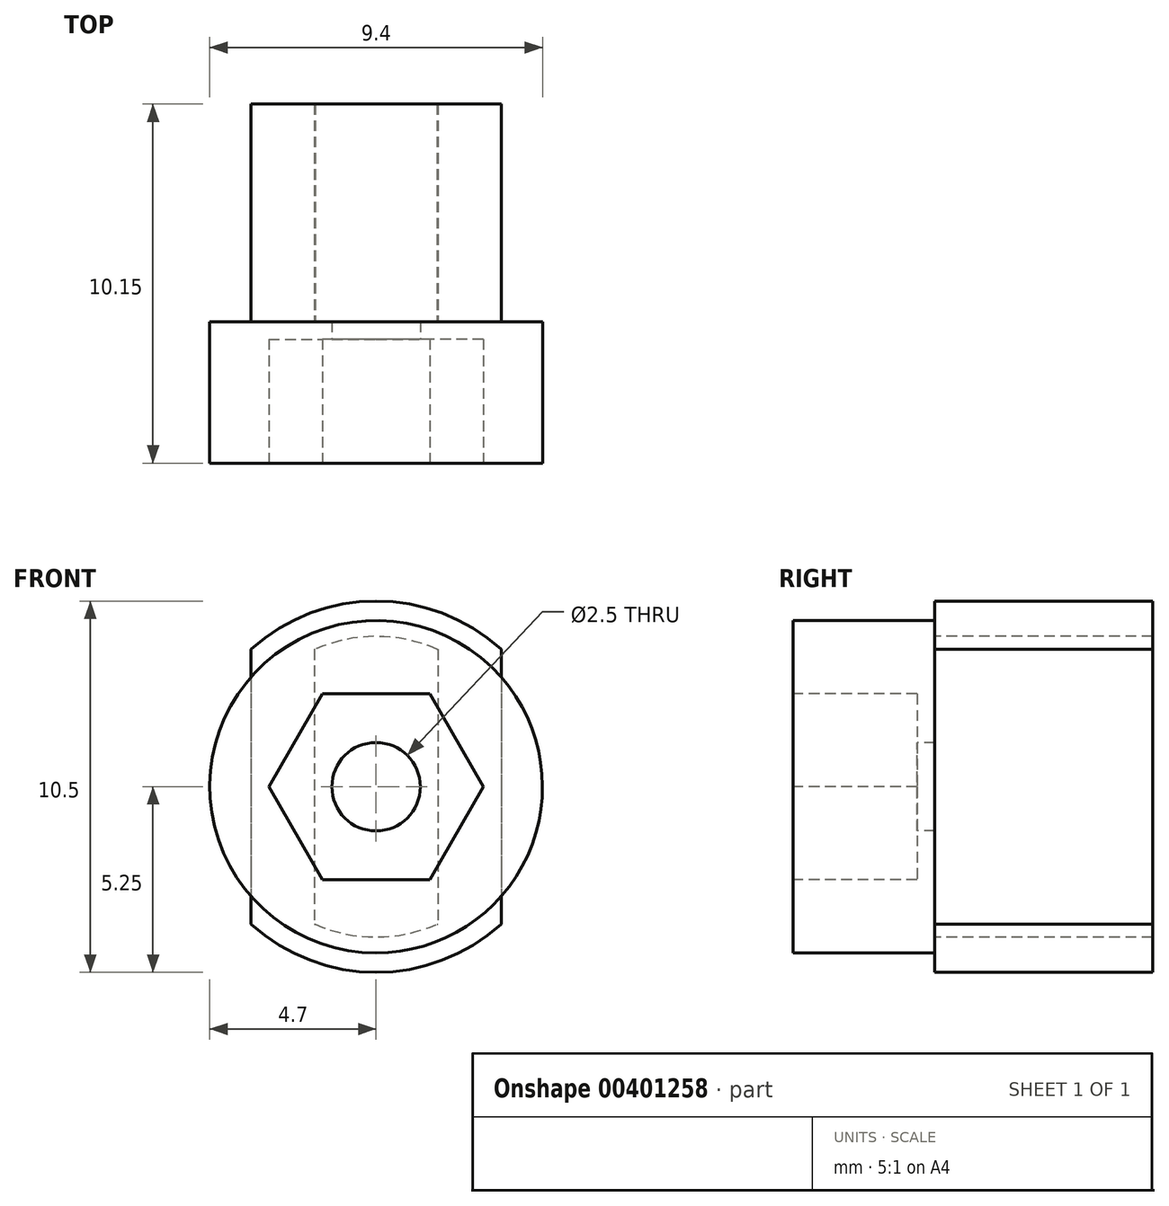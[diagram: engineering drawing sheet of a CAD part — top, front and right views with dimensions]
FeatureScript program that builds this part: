
annotation { "Feature Type Name" : "Feature", "Feature Type Description" : "" }
export const myFeature = defineFeature(function(context is Context, id is Id, definition is map)
    precondition{}
    {
        {
            var Q0;
            Q0=qCreatedBy(makeId("Front.planeOp"),FACE);
            var sketch = newSketch(context, id + "F0", { "sketchPlane" : qUnion([Q0])});
            skCircle(sketch, "E0", {"center": v(0, 0) * mm, "radius": 5.25 * mm});
            skCircle(sketch, "E1", {"center": v(0, 0) * mm, "radius": 4.25 * mm});
            skLineSegment(sketch, "E2.bottom", {"start": v(-1.75, 4.95) * mm, "end": v(1.75, 4.95) * mm});
            skLineSegment(sketch, "E2.top", {"start": v(-1.75, -4.95) * mm, "end": v(1.75, -4.95) * mm});
            skLineSegment(sketch, "E2.left", {"start": v(-1.75, 4.95) * mm, "end": v(-1.75, -4.95) * mm});
            skLineSegment(sketch, "E2.right", {"start": v(1.75, 4.95) * mm, "end": v(1.75, -4.95) * mm});
            skLineSegment(sketch, "E3.bottom", {"start": v(-3.53, 3.88) * mm, "end": v(3.53, 3.88) * mm});
            skLineSegment(sketch, "E3.top", {"start": v(-3.53, -3.88) * mm, "end": v(3.53, -3.88) * mm});
            skLineSegment(sketch, "E3.left", {"start": v(-3.53, 3.88) * mm, "end": v(-3.53, -3.88) * mm});
            skLineSegment(sketch, "E3.right", {"start": v(3.53, 3.88) * mm, "end": v(3.53, -3.88) * mm});
            skSolve(sketch);
        }
        {
            var Q0;
            {var subQ0=sQuery(id+"F0.wireOp",EDGE,"E2.left");var subQ3=sQuery(id+"F0.wireOp",EDGE,"E3.bottom");var subQ5=makeQuery(id+"F0.imprint","INTERSECT",VERTEX,{"derivedFrom":[subQ0,subQ3]});Q0=makeQuery(id+"F0.imprint","IMPRINT",FACE,{"disambiguationData":[TD([[makeQuery(id+"F0.imprint","IMPRINT",EDGE,{"disambiguationData":[TD([[subQ5,1.0]])],"derivedFrom":subQ0}),-1.0]])]});}
            var Q1;
            {var subQ0=sQuery(id+"F0.wireOp",EDGE,"E2.left");var subQ1=sQuery(id+"F0.wireOp",EDGE,"E1");var subQ2=makeQuery(id+"F0.imprint","INTERSECT",VERTEX,{"disambiguationData":[OD(0.0)],"derivedFrom":[subQ1,subQ0]});Q1=makeQuery(id+"F0.imprint","IMPRINT",FACE,{"disambiguationData":[TD([[makeQuery(id+"F0.imprint","IMPRINT",EDGE,{"disambiguationData":[TD([[subQ2,-1.0]])],"derivedFrom":subQ1}),-1.0]])]});}
            var Q2;
            {var subQ0=sQuery(id+"F0.wireOp",EDGE,"E2.left");var subQ1=sQuery(id+"F0.wireOp",EDGE,"E1");var subQ2=makeQuery(id+"F0.imprint","INTERSECT",VERTEX,{"disambiguationData":[OD(0.0)],"derivedFrom":[subQ1,subQ0]});Q2=makeQuery(id+"F0.imprint","IMPRINT",FACE,{"disambiguationData":[TD([[makeQuery(id+"F0.imprint","IMPRINT",EDGE,{"disambiguationData":[TD([[subQ2,-1.0]])],"derivedFrom":subQ1}),1.0]])]});}
            var Q3;
            {var subQ0=sQuery(id+"F0.wireOp",EDGE,"E3.left");var subQ1=sQuery(id+"F0.wireOp",EDGE,"E1");var subQ2=makeQuery(id+"F0.imprint","INTERSECT",VERTEX,{"disambiguationData":[OD(1.0)],"derivedFrom":[subQ1,subQ0]});Q3=makeQuery(id+"F0.imprint","IMPRINT",FACE,{"disambiguationData":[TD([[makeQuery(id+"F0.imprint","IMPRINT",EDGE,{"disambiguationData":[TD([[subQ2,-1.0]])],"derivedFrom":subQ1}),-1.0]])]});}
            var Q4;
            {var subQ0=sQuery(id+"F0.wireOp",EDGE,"E2.left");var subQ3=sQuery(id+"F0.wireOp",EDGE,"E3.top");var subQ5=makeQuery(id+"F0.imprint","INTERSECT",VERTEX,{"derivedFrom":[subQ0,subQ3]});Q4=makeQuery(id+"F0.imprint","IMPRINT",FACE,{"disambiguationData":[TD([[makeQuery(id+"F0.imprint","IMPRINT",EDGE,{"disambiguationData":[TD([[subQ5,-1.0]])],"derivedFrom":subQ0}),-1.0]])]});}
            var Q5;
            {var subQ1=sQuery(id+"F0.wireOp",EDGE,"E2.top");Q5=makeQuery(id+"F0.imprint","IMPRINT",FACE,{"disambiguationData":[TD([[makeQuery(id+"F0.imprint","IMPRINT",EDGE,{"derivedFrom":subQ1}),1.0]])]});}
            var Q6;
            {var subQ0=sQuery(id+"F0.wireOp",EDGE,"E2.top");Q6=makeQuery(id+"F0.imprint","IMPRINT",FACE,{"disambiguationData":[TD([[makeQuery(id+"F0.imprint","IMPRINT",EDGE,{"derivedFrom":subQ0}),-1.0]])]});}
            var Q7;
            {var subQ0=sQuery(id+"F0.wireOp",EDGE,"E2.right");var subQ3=sQuery(id+"F0.wireOp",EDGE,"E3.top");var subQ5=makeQuery(id+"F0.imprint","INTERSECT",VERTEX,{"derivedFrom":[subQ0,subQ3]});Q7=makeQuery(id+"F0.imprint","IMPRINT",FACE,{"disambiguationData":[TD([[makeQuery(id+"F0.imprint","IMPRINT",EDGE,{"disambiguationData":[TD([[subQ5,-1.0]])],"derivedFrom":subQ0}),1.0]])]});}
            var Q8;
            {var subQ0=sQuery(id+"F0.wireOp",EDGE,"E2.right");var subQ1=sQuery(id+"F0.wireOp",EDGE,"E1");var subQ2=makeQuery(id+"F0.imprint","INTERSECT",VERTEX,{"disambiguationData":[OD(1.0)],"derivedFrom":[subQ1,subQ0]});Q8=makeQuery(id+"F0.imprint","IMPRINT",FACE,{"disambiguationData":[TD([[makeQuery(id+"F0.imprint","IMPRINT",EDGE,{"disambiguationData":[TD([[subQ2,-1.0]])],"derivedFrom":subQ1}),-1.0]])]});}
            var Q9;
            {var subQ0=sQuery(id+"F0.wireOp",EDGE,"E2.right");var subQ1=sQuery(id+"F0.wireOp",EDGE,"E1");var subQ2=makeQuery(id+"F0.imprint","INTERSECT",VERTEX,{"disambiguationData":[OD(0.0)],"derivedFrom":[subQ1,subQ0]});Q9=makeQuery(id+"F0.imprint","IMPRINT",FACE,{"disambiguationData":[TD([[makeQuery(id+"F0.imprint","IMPRINT",EDGE,{"disambiguationData":[TD([[subQ2,1.0]])],"derivedFrom":subQ1}),1.0]])]});}
            var Q10;
            {var subQ0=sQuery(id+"F0.wireOp",EDGE,"E2.right");var subQ1=sQuery(id+"F0.wireOp",EDGE,"E1");var subQ2=makeQuery(id+"F0.imprint","INTERSECT",VERTEX,{"disambiguationData":[OD(0.0)],"derivedFrom":[subQ1,subQ0]});Q10=makeQuery(id+"F0.imprint","IMPRINT",FACE,{"disambiguationData":[TD([[makeQuery(id+"F0.imprint","IMPRINT",EDGE,{"disambiguationData":[TD([[subQ2,1.0]])],"derivedFrom":subQ1}),-1.0]])]});}
            var Q11;
            {var subQ0=sQuery(id+"F0.wireOp",EDGE,"E2.right");var subQ3=sQuery(id+"F0.wireOp",EDGE,"E3.bottom");var subQ5=makeQuery(id+"F0.imprint","INTERSECT",VERTEX,{"derivedFrom":[subQ0,subQ3]});Q11=makeQuery(id+"F0.imprint","IMPRINT",FACE,{"disambiguationData":[TD([[makeQuery(id+"F0.imprint","IMPRINT",EDGE,{"disambiguationData":[TD([[subQ5,1.0]])],"derivedFrom":subQ0}),1.0]])]});}
            var Q12;
            {var subQ1=sQuery(id+"F0.wireOp",EDGE,"E2.bottom");Q12=makeQuery(id+"F0.imprint","IMPRINT",FACE,{"disambiguationData":[TD([[makeQuery(id+"F0.imprint","IMPRINT",EDGE,{"derivedFrom":subQ1}),-1.0]])]});}
            var Q13;
            {var subQ0=sQuery(id+"F0.wireOp",EDGE,"E2.bottom");Q13=makeQuery(id+"F0.imprint","IMPRINT",FACE,{"disambiguationData":[TD([[makeQuery(id+"F0.imprint","IMPRINT",EDGE,{"derivedFrom":subQ0}),1.0]])]});}
            extrude(context, id + "F1", {"entities" : qUnion([Q0, Q1, Q2, Q3, Q4, Q5, Q6, Q7, Q8, Q9, Q10, Q11, Q12, Q13]), "oppositeDirection" : true, "depth" : 6.15 * mm});
        }
        {
            var Q0;
            Q0=qCreatedBy(makeId("Front.planeOp"),FACE);
            var sketch = newSketch(context, id + "F2", { "sketchPlane" : qUnion([Q0])});
            skCircle(sketch, "E4", {"center": v(0, 0) * mm, "radius": 4.7 * mm});
            skSolve(sketch);
        }
        {
            var Q0;
            Q0=makeQuery(id+"F2.imprint","IMPRINT",FACE,{"disambiguationData":[TD([[makeQuery(id+"F2.imprint","IMPRINT",EDGE,{"derivedFrom":sQuery(id+"F2.wireOp",EDGE,"E4")}),1.0]])]});
            extrude(context, id + "F3", {"entities" : qUnion([Q0]), "operationType" : NewBodyOperationType.ADD, "depth" : 4 * mm});
        }
        {
            var Q0;
            Q0=makeQuery(id+"F3.opExtrude","CAP_FACE",FACE,{"disambiguationData":[OSD([sQuery(id+"F2.wireOp",EDGE,"E4")])],"isStart":false});
            cPlane(context, id + "F4", {"entities" : qUnion([Q0]), "cplaneType" : CPlaneType.OFFSET, "offset" : 0 * mm, "width" : 150 * mm, "height" : 150 * mm});
        }
        {
            var Q0;
            Q0=qCreatedBy(id+"F4.planeOp",FACE);
            var sketch = newSketch(context, id + "F5", { "sketchPlane" : qUnion([Q0])});
            skCircle(sketch, "E5.cCircle", {"center": v(0, 0) * mm, "radius": 2.62 * mm, "construction": true});
            skLineSegment(sketch, "E5.0", {"start": v(1.52, -2.62) * mm, "end": v(-1.52, -2.62) * mm});
            skLineSegment(sketch, "E5.1", {"start": v(-1.52, -2.62) * mm, "end": v(-3.03, 0) * mm});
            skLineSegment(sketch, "E5.2", {"start": v(-3.03, 0) * mm, "end": v(-1.52, 2.62) * mm});
            skLineSegment(sketch, "E5.3", {"start": v(-1.52, 2.62) * mm, "end": v(1.52, 2.63) * mm});
            skLineSegment(sketch, "E5.4", {"start": v(1.52, 2.63) * mm, "end": v(3.03, 0) * mm});
            skLineSegment(sketch, "E5.5", {"start": v(3.03, 0) * mm, "end": v(1.52, -2.62) * mm});
            skPoint(sketch, "E5.0.midPoint", {"position": v(0, -2.62) * mm});
            skSolve(sketch);
        }
        {
            var Q0;
            Q0=makeQuery(id+"F5.imprint","IMPRINT",FACE,{"disambiguationData":[TD([[makeQuery(id+"F5.imprint","IMPRINT",EDGE,{"derivedFrom":sQuery(id+"F5.wireOp",EDGE,"E5.0")}),-1.0]])]});
            extrude(context, id + "F6", {"entities" : qUnion([Q0]), "operationType" : NewBodyOperationType.REMOVE, "oppositeDirection" : true, "depth" : 3.5 * mm});
        }
        {
            var Q0;
            Q0=qCreatedBy(id+"F4.planeOp",FACE);
            var sketch = newSketch(context, id + "F7", { "sketchPlane" : qUnion([Q0])});
            skCircle(sketch, "E6", {"center": v(0, 0) * mm, "radius": 1.25 * mm});
            skSolve(sketch);
        }
        {
            var Q0;
            Q0=makeQuery(id+"F7.imprint","IMPRINT",FACE,{"disambiguationData":[TD([[makeQuery(id+"F7.imprint","IMPRINT",EDGE,{"derivedFrom":sQuery(id+"F7.wireOp",EDGE,"E6")}),1.0]])]});
            extrude(context, id + "F8", {"entities" : qUnion([Q0]), "operationType" : NewBodyOperationType.REMOVE, "oppositeDirection" : true, "depth" : 5 * mm});
        }
    });
